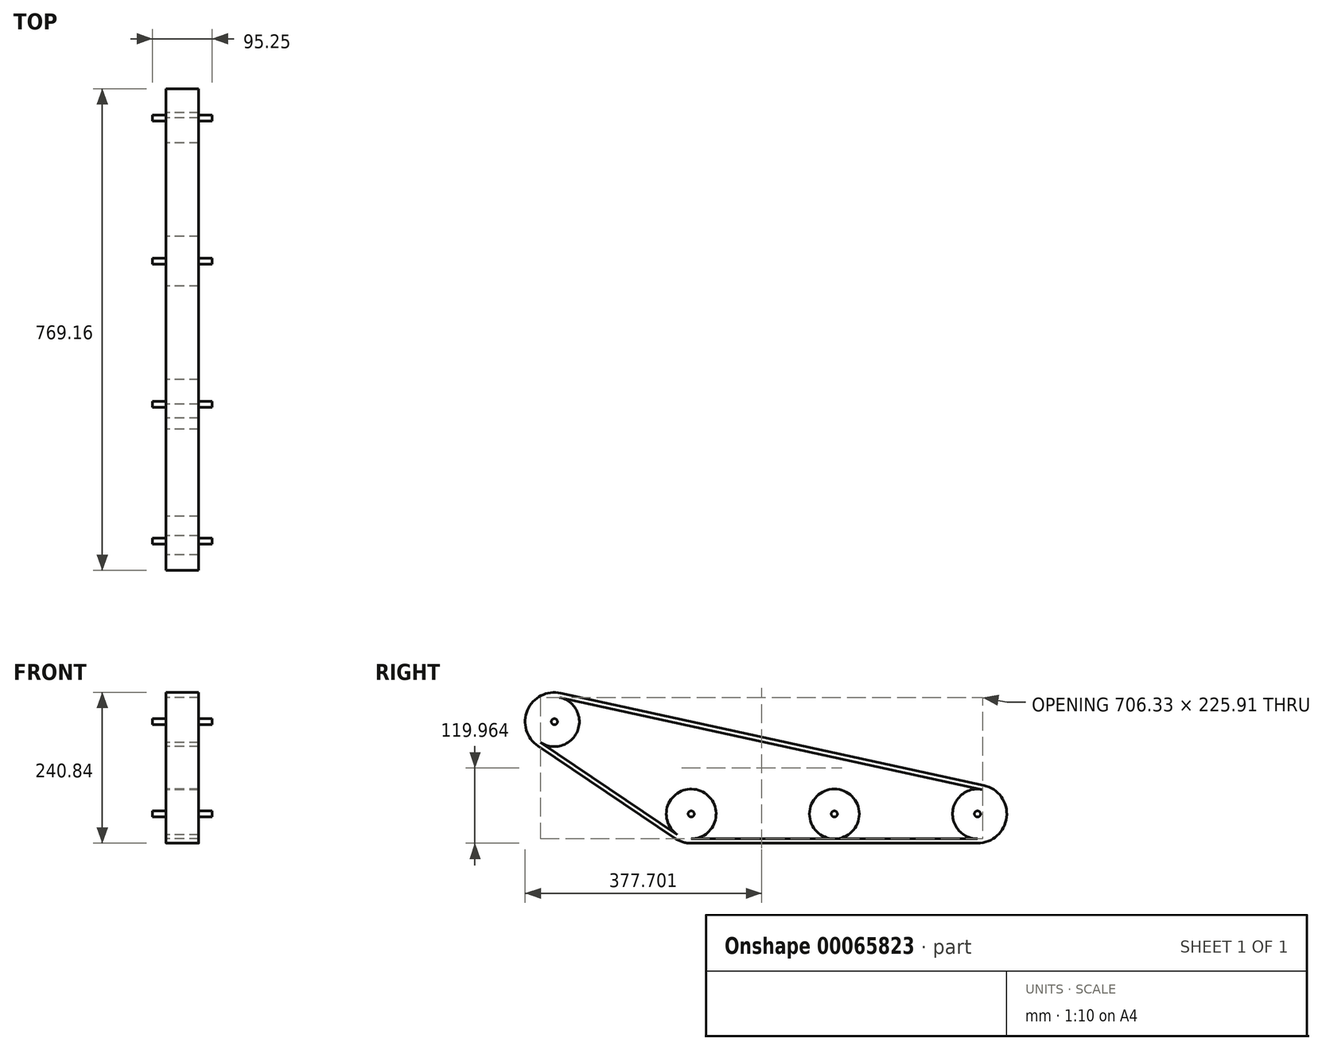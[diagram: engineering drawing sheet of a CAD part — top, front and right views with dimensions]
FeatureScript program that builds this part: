
annotation { "Feature Type Name" : "Feature", "Feature Type Description" : "" }
export const myFeature = defineFeature(function(context is Context, id is Id, definition is map)
    precondition{}
    {
        {
            var Q0;
            Q0=qCreatedBy(makeId("Right.planeOp"),FACE);
            var sketch = newSketch(context, id + "F0", { "sketchPlane" : qUnion([Q0])});
            skCircle(sketch, "E0", {"center": v(0, 0) * mm, "radius": 39.75 * mm});
            skCircle(sketch, "E1", {"center": v(228.6, 0) * mm, "radius": 39.75 * mm});
            skCircle(sketch, "E2", {"center": v(457.2, 0) * mm, "radius": 39.75 * mm});
            skLineSegment(sketch, "E3", {"start": v(0, -39.75) * mm, "end": v(457.2, -39.75) * mm});
            skLineSegment(sketch, "E4.0", {"start": v(0, -46.76) * mm, "end": v(457.2, -46.76) * mm});
            skCircle(sketch, "E5", {"center": v(-218.44, 147.32) * mm, "radius": 39.75 * mm});
            skLineSegment(sketch, "E6", {"start": v(-240.67, 114.36) * mm, "end": v(-22.23, -32.96) * mm});
            skLineSegment(sketch, "E7.0", {"start": v(-244.59, 108.55) * mm, "end": v(-26.15, -38.77) * mm});
            skArc(sketch, "E8.0", {"start": v(-26.15, -38.77) * mm, "mid": v(-13.67, -44.72) * mm, "end": v(0, -46.76) * mm});
            skLineSegment(sketch, "E9", {"start": v(-209.97, 186.16) * mm, "end": v(465.67, 38.84) * mm});
            skLineSegment(sketch, "E10.0", {"start": v(-208.48, 193) * mm, "end": v(467.16, 45.69) * mm});
            skArc(sketch, "E11.0", {"start": v(457.2, -46.76) * mm, "mid": v(503.7, -5) * mm, "end": v(467.16, 45.69) * mm});
            skArc(sketch, "E12.0", {"start": v(-208.48, 193) * mm, "mid": v(-261.44, 165.7) * mm, "end": v(-244.59, 108.55) * mm});
            skSolve(sketch);
        }
        {
            var Q0;
            Q0=makeQuery(id+"F0.imprint","IMPRINT",FACE,{"disambiguationData":[TD([[makeQuery(id+"F0.imprint","IMPRINT",EDGE,{"derivedFrom":sQuery(id+"F0.wireOp",EDGE,"E4.0")}),1.0]])]});
            var Q1;
            Q1=makeQuery(id+"F0.imprint","IMPRINT",FACE,{"disambiguationData":[TD([[makeQuery(id+"F0.imprint","IMPRINT",EDGE,{"derivedFrom":sQuery(id+"F0.wireOp",EDGE,"E1")}),1.0]])]});
            var Q2;
            {var subQ0=sQuery(id+"F0.wireOp",EDGE,"E2");var subQ1=makeQuery(id+"F0.imprint","INTERSECT",VERTEX,{"derivedFrom":[subQ0,sQuery(id+"F0.wireOp",EDGE,"E3")]});Q2=makeQuery(id+"F0.imprint","IMPRINT",FACE,{"disambiguationData":[TD([[makeQuery(id+"F0.imprint","IMPRINT",EDGE,{"disambiguationData":[TD([[subQ1,1.0]])],"derivedFrom":subQ0}),1.0]])]});}
            var Q3;
            {var subQ0=sQuery(id+"F0.wireOp",EDGE,"E0");var subQ1=makeQuery(id+"F0.imprint","INTERSECT",VERTEX,{"derivedFrom":[subQ0,sQuery(id+"F0.wireOp",EDGE,"E3")]});Q3=makeQuery(id+"F0.imprint","IMPRINT",FACE,{"disambiguationData":[TD([[makeQuery(id+"F0.imprint","IMPRINT",EDGE,{"disambiguationData":[TD([[subQ1,1.0]])],"derivedFrom":subQ0}),1.0]])]});}
            var Q4;
            {var subQ0=sQuery(id+"F0.wireOp",EDGE,"E5");var subQ1=makeQuery(id+"F0.imprint","INTERSECT",VERTEX,{"derivedFrom":[subQ0,sQuery(id+"F0.wireOp",EDGE,"E6")]});Q4=makeQuery(id+"F0.imprint","IMPRINT",FACE,{"disambiguationData":[TD([[makeQuery(id+"F0.imprint","IMPRINT",EDGE,{"disambiguationData":[TD([[subQ1,1.0]])],"derivedFrom":subQ0}),1.0]])]});}
            extrude(context, id + "F1", {"entities" : qUnion([Q0, Q1, Q2, Q3, Q4]), "depth" : 52.07 * mm});
        }
        {
            var Q0;
            Q0=makeQuery(id+"F1.opExtrude","CAP_FACE",FACE,{"disambiguationData":[OSD([sQuery(id+"F0.wireOp",EDGE,"E0"),sQuery(id+"F0.wireOp",EDGE,"E2"),sQuery(id+"F0.wireOp",EDGE,"E3"),sQuery(id+"F0.wireOp",EDGE,"E4.0"),sQuery(id+"F0.wireOp",EDGE,"E5"),sQuery(id+"F0.wireOp",EDGE,"E6"),sQuery(id+"F0.wireOp",EDGE,"E7.0"),sQuery(id+"F0.wireOp",EDGE,"E8.0"),sQuery(id+"F0.wireOp",EDGE,"E9"),sQuery(id+"F0.wireOp",EDGE,"E10.0"),sQuery(id+"F0.wireOp",EDGE,"E11.0"),sQuery(id+"F0.wireOp",EDGE,"E12.0")])],"isStart":false});
            var sketch = newSketch(context, id + "F2", { "sketchPlane" : qUnion([Q0])});
            skCircle(sketch, "E13", {"center": v(-218.44, 147.32) * mm, "radius": 4.83 * mm});
            skCircle(sketch, "E14", {"center": v(0, 0) * mm, "radius": 4.83 * mm});
            skCircle(sketch, "E15", {"center": v(457.2, 0) * mm, "radius": 4.83 * mm});
            skCircle(sketch, "E16", {"center": v(228.6, 0) * mm, "radius": 4.83 * mm});
            skSolve(sketch);
        }
        {
            var Q0;
            Q0=makeQuery(id+"F2.imprint","IMPRINT",FACE,{"disambiguationData":[TD([[makeQuery(id+"F2.imprint","IMPRINT",EDGE,{"derivedFrom":sQuery(id+"F2.wireOp",EDGE,"E13")}),1.0]])]});
            var Q1;
            Q1=makeQuery(id+"F2.imprint","IMPRINT",FACE,{"disambiguationData":[TD([[makeQuery(id+"F2.imprint","IMPRINT",EDGE,{"derivedFrom":sQuery(id+"F2.wireOp",EDGE,"E14")}),1.0]])]});
            var Q2;
            Q2=makeQuery(id+"F2.imprint","IMPRINT",FACE,{"disambiguationData":[TD([[makeQuery(id+"F2.imprint","IMPRINT",EDGE,{"derivedFrom":sQuery(id+"F2.wireOp",EDGE,"E16")}),1.0]])]});
            var Q3;
            Q3=makeQuery(id+"F2.imprint","IMPRINT",FACE,{"disambiguationData":[TD([[makeQuery(id+"F2.imprint","IMPRINT",EDGE,{"derivedFrom":sQuery(id+"F2.wireOp",EDGE,"E15")}),1.0]])]});
            extrude(context, id + "F3", {"entities" : qUnion([Q0, Q1, Q2, Q3]), "depth" : 21.59 * mm});
        }
        {
            var Q0;
            Q0=makeQuery(id+"F1.opExtrude","CAP_FACE",FACE,{"disambiguationData":[OSD([sQuery(id+"F0.wireOp",EDGE,"E0"),sQuery(id+"F0.wireOp",EDGE,"E2"),sQuery(id+"F0.wireOp",EDGE,"E3"),sQuery(id+"F0.wireOp",EDGE,"E4.0"),sQuery(id+"F0.wireOp",EDGE,"E5"),sQuery(id+"F0.wireOp",EDGE,"E6"),sQuery(id+"F0.wireOp",EDGE,"E7.0"),sQuery(id+"F0.wireOp",EDGE,"E8.0"),sQuery(id+"F0.wireOp",EDGE,"E9"),sQuery(id+"F0.wireOp",EDGE,"E10.0"),sQuery(id+"F0.wireOp",EDGE,"E11.0"),sQuery(id+"F0.wireOp",EDGE,"E12.0")])],"isStart":true});
            var sketch = newSketch(context, id + "F4", { "sketchPlane" : qUnion([Q0])});
            skCircle(sketch, "E17", {"center": v(-457.2, 0) * mm, "radius": 4.83 * mm});
            skCircle(sketch, "E18", {"center": v(0, 0) * mm, "radius": 4.83 * mm});
            skCircle(sketch, "E19", {"center": v(218.44, 147.32) * mm, "radius": 4.83 * mm});
            skCircle(sketch, "E20", {"center": v(-228.6, 0) * mm, "radius": 4.83 * mm});
            skSolve(sketch);
        }
        {
            var Q0;
            Q0=makeQuery(id+"F4.imprint","IMPRINT",FACE,{"disambiguationData":[TD([[makeQuery(id+"F4.imprint","IMPRINT",EDGE,{"derivedFrom":sQuery(id+"F4.wireOp",EDGE,"E17")}),1.0]])]});
            var Q1;
            Q1=makeQuery(id+"F4.imprint","IMPRINT",FACE,{"disambiguationData":[TD([[makeQuery(id+"F4.imprint","IMPRINT",EDGE,{"derivedFrom":sQuery(id+"F4.wireOp",EDGE,"E20")}),1.0]])]});
            var Q2;
            Q2=makeQuery(id+"F4.imprint","IMPRINT",FACE,{"disambiguationData":[TD([[makeQuery(id+"F4.imprint","IMPRINT",EDGE,{"derivedFrom":sQuery(id+"F4.wireOp",EDGE,"E18")}),1.0]])]});
            var Q3;
            Q3=makeQuery(id+"F4.imprint","IMPRINT",FACE,{"disambiguationData":[TD([[makeQuery(id+"F4.imprint","IMPRINT",EDGE,{"derivedFrom":sQuery(id+"F4.wireOp",EDGE,"E19")}),1.0]])]});
            extrude(context, id + "F5", {"entities" : qUnion([Q0, Q1, Q2, Q3]), "depth" : 21.59 * mm});
        }
    });
